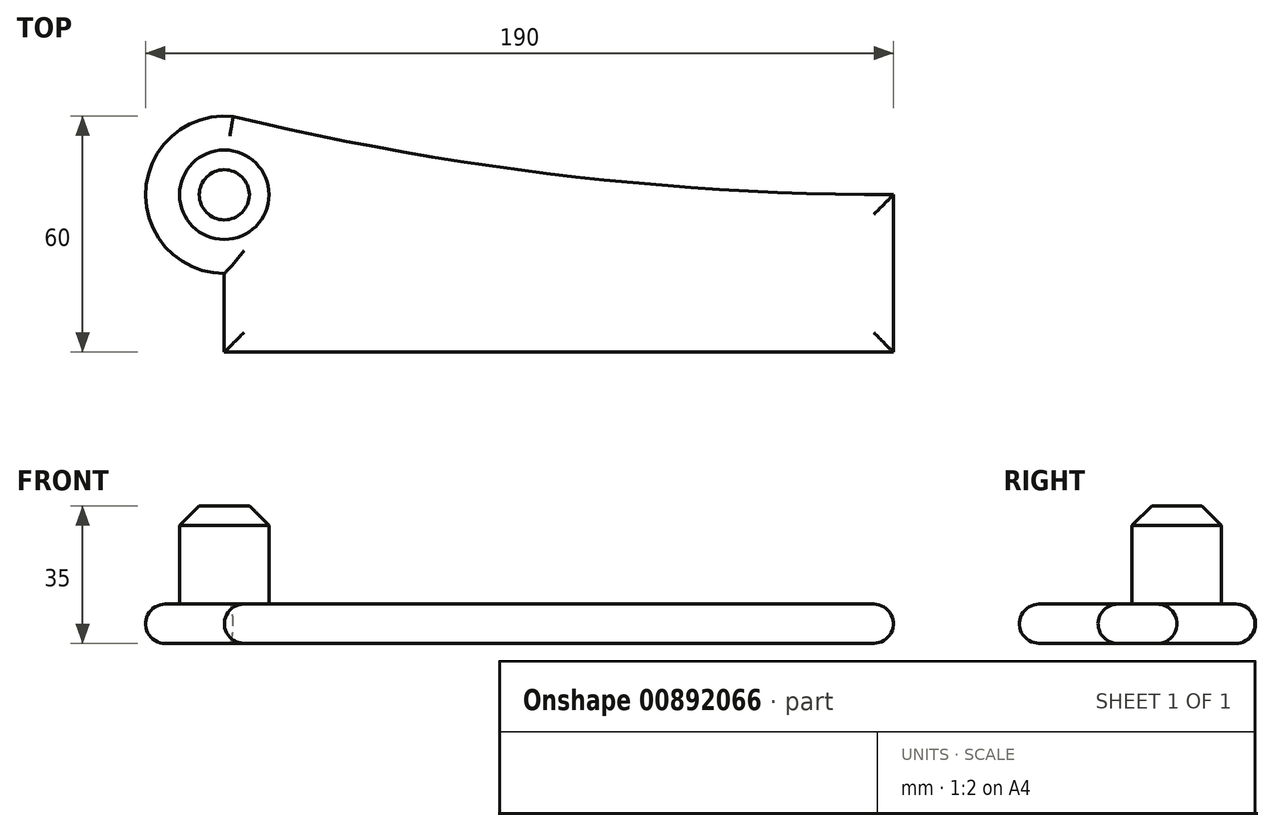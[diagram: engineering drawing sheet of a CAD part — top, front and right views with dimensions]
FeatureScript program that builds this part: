
annotation { "Feature Type Name" : "Feature", "Feature Type Description" : "" }
export const myFeature = defineFeature(function(context is Context, id is Id, definition is map)
    precondition{}
    {
        {
            var Q0;
            Q0=qCreatedBy(makeId("Top.planeOp"),FACE);
            var sketch = newSketch(context, id + "F0", { "sketchPlane" : qUnion([Q0])});
            skLineSegment(sketch, "E0.bottom", {"start": v(-85, -20) * mm, "end": v(85, -20) * mm});
            skLineSegment(sketch, "E0.top", {"start": v(-85, 20) * mm, "end": v(85, 20) * mm});
            skLineSegment(sketch, "E0.left", {"start": v(-85, -20) * mm, "end": v(-85, 20) * mm});
            skLineSegment(sketch, "E0.right", {"start": v(85, -20) * mm, "end": v(85, 20) * mm});
            skPoint(sketch, "E0.middle", {"position": v(0, 0) * mm});
            skCircle(sketch, "E1", {"center": v(-85, 20) * mm, "radius": 20 * mm});
            skArc(sketch, "E2", {"start": v(-82.74, 39.87) * mm, "mid": v(0.54, 24.99) * mm, "end": v(85, 20) * mm});
            skSolve(sketch);
        }
        {
            var Q0;
            {var subQ3=sQuery(id+"F0.wireOp",EDGE,"E0.left");var subQ5=sQuery(id+"F0.wireOp",EDGE,"E0.top");var subQ6=makeQuery(id+"F0.imprint","INTERSECT",VERTEX,{"derivedFrom":[subQ5,subQ3]});Q0=makeQuery(id+"F0.imprint","IMPRINT",FACE,{"disambiguationData":[TD([[makeQuery(id+"F0.imprint","IMPRINT",EDGE,{"disambiguationData":[TD([[subQ6,-1.0]])],"derivedFrom":subQ5}),1.0]])]});}
            var Q1;
            {var subQ0=sQuery(id+"F0.wireOp",EDGE,"E2");var subQ3=sQuery(id+"F0.wireOp",EDGE,"E1");var subQ5=makeQuery(id+"F0.imprint","INTERSECT",VERTEX,{"disambiguationData":[OD(1.0)],"derivedFrom":[subQ3,subQ0]});Q1=makeQuery(id+"F0.imprint","IMPRINT",FACE,{"disambiguationData":[TD([[makeQuery(id+"F0.imprint","IMPRINT",EDGE,{"disambiguationData":[TD([[subQ5,1.0]])],"derivedFrom":subQ3}),-1.0]])]});}
            var Q2;
            {var subQ1=sQuery(id+"F0.wireOp",EDGE,"E0.bottom");Q2=makeQuery(id+"F0.imprint","IMPRINT",FACE,{"disambiguationData":[TD([[makeQuery(id+"F0.imprint","IMPRINT",EDGE,{"derivedFrom":subQ1}),1.0]])]});}
            var Q3;
            {var subQ0=sQuery(id+"F0.wireOp",EDGE,"E0.left");var subQ1=sQuery(id+"F0.wireOp",EDGE,"E0.top");var subQ2=makeQuery(id+"F0.imprint","INTERSECT",VERTEX,{"derivedFrom":[subQ1,subQ0]});Q3=makeQuery(id+"F0.imprint","IMPRINT",FACE,{"disambiguationData":[TD([[makeQuery(id+"F0.imprint","IMPRINT",EDGE,{"disambiguationData":[TD([[subQ2,-1.0]])],"derivedFrom":subQ1}),-1.0]])]});}
            extrude(context, id + "F1", {"entities" : qUnion([Q0, Q1, Q2, Q3]), "depth" : 10 * mm, "offsetDistance" : 25 * mm});
        }
        {
            var Q0;
            Q0=makeQuery(id+"F1.opExtrude","CAP_EDGE",EDGE,{"disambiguationData":[OSD([sQuery(id+"F0.wireOp",EDGE,"E1")])],"isStart":false});
            var Q1;
            Q1=makeQuery(id+"F1.opExtrude","CAP_EDGE",EDGE,{"disambiguationData":[OSD([sQuery(id+"F0.wireOp",EDGE,"E2")])],"isStart":false});
            var Q2;
            Q2=makeQuery(id+"F1.opExtrude","CAP_FACE",FACE,{"disambiguationData":[OSD([sQuery(id+"F0.wireOp",EDGE,"E0.bottom"),sQuery(id+"F0.wireOp",EDGE,"E0.left"),sQuery(id+"F0.wireOp",EDGE,"E0.right"),sQuery(id+"F0.wireOp",EDGE,"E1"),sQuery(id+"F0.wireOp",EDGE,"E2")])],"isStart":false});
            var Q3;
            Q3=makeQuery(id+"F1.opExtrude","CAP_FACE",FACE,{"disambiguationData":[OSD([sQuery(id+"F0.wireOp",EDGE,"E0.bottom"),sQuery(id+"F0.wireOp",EDGE,"E0.left"),sQuery(id+"F0.wireOp",EDGE,"E0.right"),sQuery(id+"F0.wireOp",EDGE,"E1"),sQuery(id+"F0.wireOp",EDGE,"E2")])],"isStart":true});
            fillet(context, id + "F2", {"entities" : qUnion([Q0, Q1, Q2, Q3]), "radius" : 5 * mm, "tangentPropagation" : true, "allowEdgeOverflow" : false});
        }
        {
            var Q0;
            Q0=makeQuery(id+"F1.opExtrude","CAP_FACE",FACE,{"disambiguationData":[OSD([sQuery(id+"F0.wireOp",EDGE,"E0.bottom"),sQuery(id+"F0.wireOp",EDGE,"E0.left"),sQuery(id+"F0.wireOp",EDGE,"E0.right"),sQuery(id+"F0.wireOp",EDGE,"E1"),sQuery(id+"F0.wireOp",EDGE,"E2")])],"isStart":false});
            var sketch = newSketch(context, id + "F3", { "sketchPlane" : qUnion([Q0])});
            skCircle(sketch, "E3", {"center": v(-85, 20) * mm, "radius": 11.37 * mm});
            skSolve(sketch);
        }
        {
            var Q0;
            Q0=makeQuery(id+"F3.imprint","IMPRINT",FACE,{"disambiguationData":[TD([[makeQuery(id+"F3.imprint","IMPRINT",EDGE,{"derivedFrom":sQuery(id+"F3.wireOp",EDGE,"E3")}),1.0]])]});
            extrude(context, id + "F4", {"entities" : qUnion([Q0]), "operationType" : NewBodyOperationType.ADD, "depth" : 25 * mm, "offsetDistance" : 25 * mm});
        }
        {
            var Q0;
            Q0=makeQuery(id+"F4.opExtrude","CAP_EDGE",EDGE,{"disambiguationData":[OSD([sQuery(id+"F3.wireOp",EDGE,"E3")])],"isStart":false});
            chamfer(context, id + "F5", {"entities" : qUnion([Q0]), "width" : 5 * mm, "tangentPropagation" : true});
        }
    });
